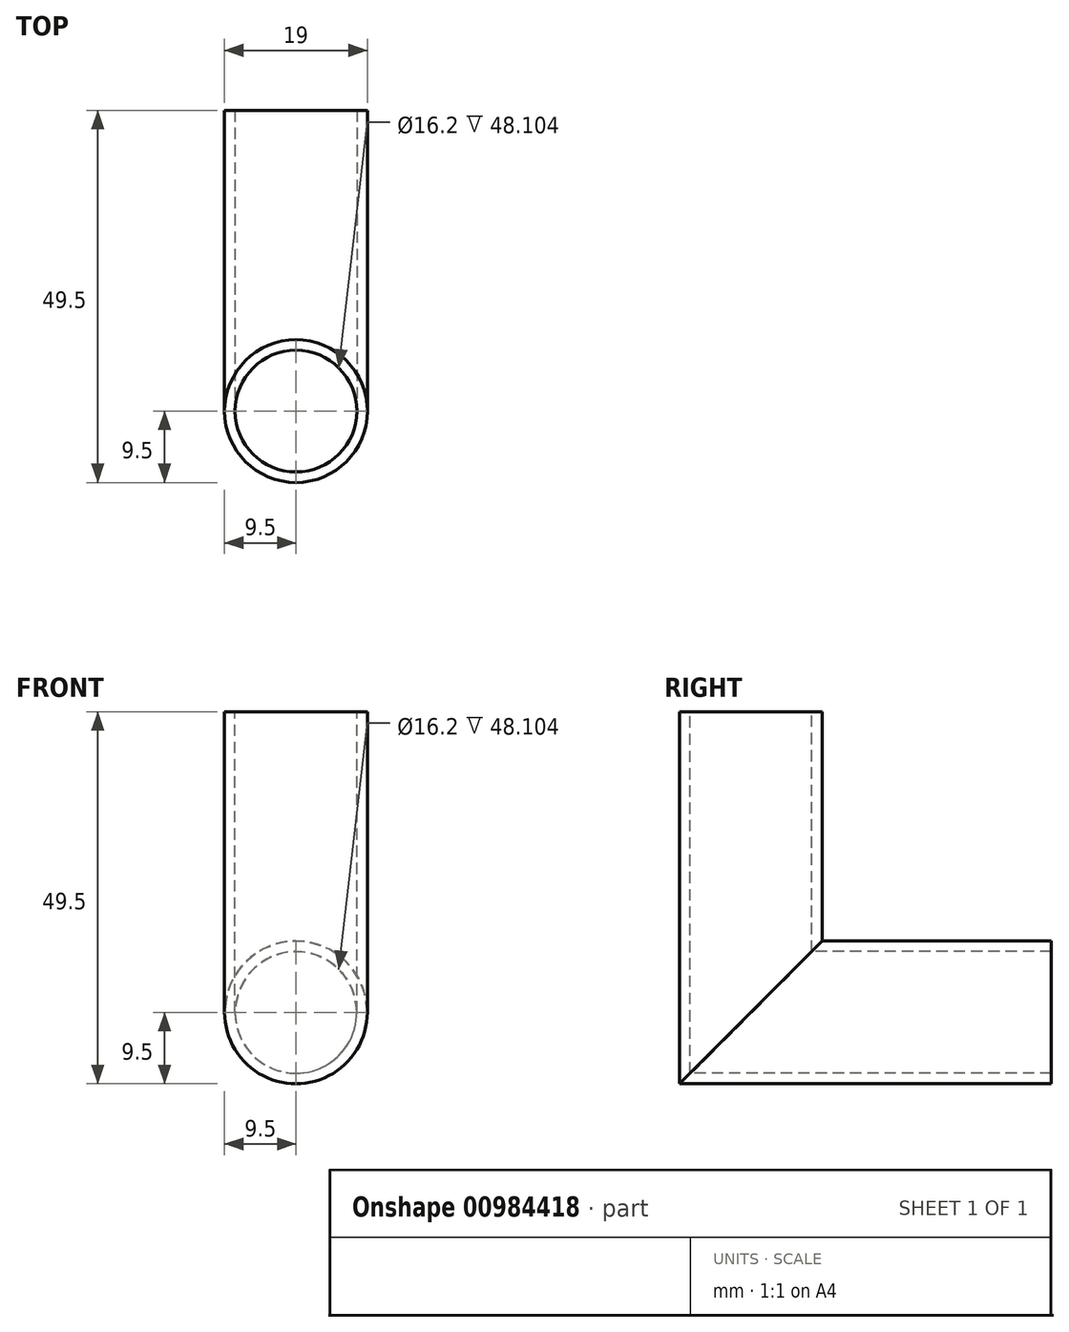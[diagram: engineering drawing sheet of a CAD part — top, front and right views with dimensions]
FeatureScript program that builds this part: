
annotation { "Feature Type Name" : "Feature", "Feature Type Description" : "" }
export const myFeature = defineFeature(function(context is Context, id is Id, definition is map)
    precondition{}
    {
        {
            var Q0;
            Q0=qCreatedBy(makeId("Front.planeOp"),FACE);
            var sketch = newSketch(context, id + "F0", { "sketchPlane" : qUnion([Q0])});
            skCircle(sketch, "E0", {"center": v(0, 0) * mm, "radius": 8.1 * mm});
            skCircle(sketch, "E1", {"center": v(0, 0) * mm, "radius": 9.5 * mm});
            skSolve(sketch);
        }
        {
            var Q0;
            Q0=qCreatedBy(makeId("Right.planeOp"),FACE);
            var sketch = newSketch(context, id + "F1", { "sketchPlane" : qUnion([Q0])});
            skLineSegment(sketch, "E2", {"start": v(-40, 0) * mm, "end": v(-40, 40) * mm});
            skLineSegment(sketch, "E3", {"start": v(-40, 0) * mm, "end": v(0, 0) * mm});
            skSolve(sketch);
        }
        {
            var Q0;
            Q0=makeQuery(id+"F0.imprint","IMPRINT",FACE,{"disambiguationData":[TD([[makeQuery(id+"F0.imprint","IMPRINT",EDGE,{"derivedFrom":sQuery(id+"F0.wireOp",EDGE,"E0")}),-1.0]])]});
            var Q1;
            Q1=sQuery(id+"F1.wireOp",EDGE,"E3");
            var Q2;
            Q2=sQuery(id+"F1.wireOp",EDGE,"E2");
            sweep(context, id + "F2", {"profiles" : qUnion([Q0]), "path" : qUnion([Q1, Q2])});
        }
    });
